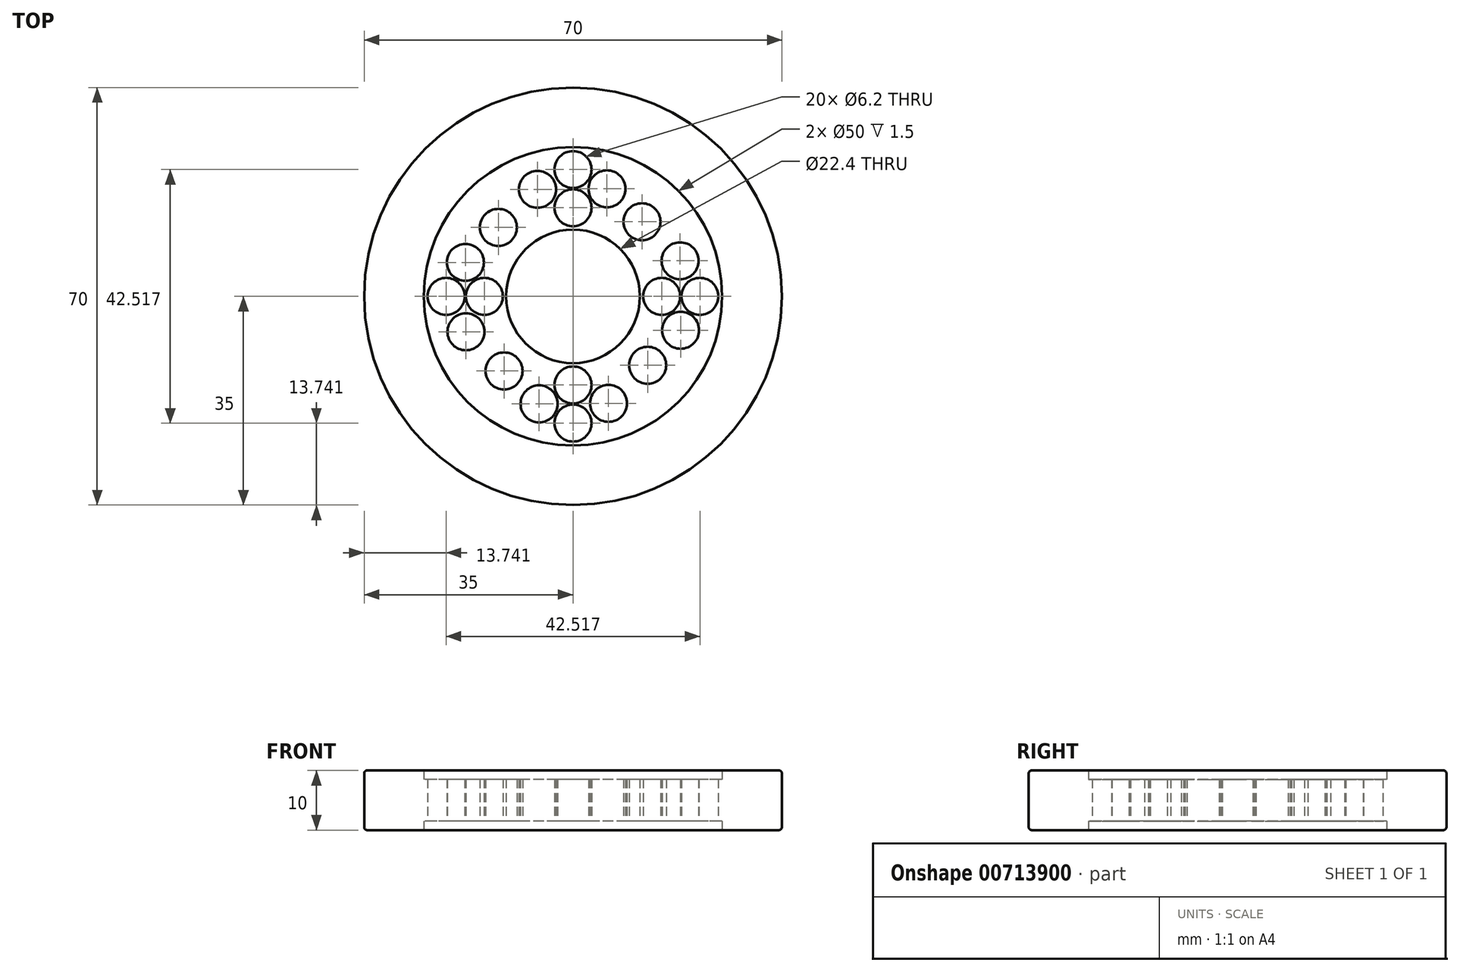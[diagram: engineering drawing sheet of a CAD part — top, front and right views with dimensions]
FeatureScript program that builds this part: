
annotation { "Feature Type Name" : "Feature", "Feature Type Description" : "" }
export const myFeature = defineFeature(function(context is Context, id is Id, definition is map)
    precondition{}
    {
        {
            var Q0;
            Q0=qCreatedBy(makeId("Top.planeOp"),FACE);
            var sketch = newSketch(context, id + "F0", { "sketchPlane" : qUnion([Q0])});
            skCircle(sketch, "E0", {"center": v(0, 0) * mm, "radius": 25 * mm});
            skCircle(sketch, "E1", {"center": v(0, 0) * mm, "radius": 35 * mm});
            skSolve(sketch);
        }
        {
            var Q0;
            Q0=qCreatedBy(makeId("Top.planeOp"),FACE);
            var sketch = newSketch(context, id + "F1", { "sketchPlane" : qUnion([Q0])});
            skCircle(sketch, "E2", {"center": v(0, 0) * mm, "radius": 11.2 * mm});
            skCircle(sketch, "E3", {"center": v(0, 0) * mm, "radius": 25 * mm});
            skCircle(sketch, "E4", {"center": v(-21.26, 0) * mm, "radius": 3.1 * mm});
            skCircle(sketch, "E5.1.0", {"center": v(0, -21.26) * mm, "radius": 3.1 * mm});
            skCircle(sketch, "E5.2.0", {"center": v(21.26, 0) * mm, "radius": 3.1 * mm});
            skCircle(sketch, "E5.3.0", {"center": v(0, 21.26) * mm, "radius": 3.1 * mm});
            skCircle(sketch, "E6", {"center": v(-14.86, 0) * mm, "radius": 3.1 * mm});
            skCircle(sketch, "E7.1.0", {"center": v(0, -14.86) * mm, "radius": 3.1 * mm});
            skCircle(sketch, "E7.2.0", {"center": v(14.86, 0) * mm, "radius": 3.1 * mm});
            skCircle(sketch, "E7.3.0", {"center": v(0, 14.86) * mm, "radius": 3.1 * mm});
            skCircle(sketch, "E8", {"center": v(-12.5, 11.56) * mm, "radius": 3.1 * mm});
            skCircle(sketch, "E9", {"center": v(-5.95, 17.94) * mm, "radius": 3.1 * mm});
            skCircle(sketch, "E10", {"center": v(-18.03, 5.7) * mm, "radius": 3.1 * mm});
            skCircle(sketch, "E11.1.0", {"center": v(-11.56, -12.5) * mm, "radius": 3.1 * mm});
            skCircle(sketch, "E11.2.0", {"center": v(12.5, -11.56) * mm, "radius": 3.1 * mm});
            skCircle(sketch, "E11.3.0", {"center": v(11.56, 12.5) * mm, "radius": 3.1 * mm});
            skCircle(sketch, "E12.1.0", {"center": v(-5.7, -18.03) * mm, "radius": 3.1 * mm});
            skCircle(sketch, "E12.2.0", {"center": v(18.03, -5.7) * mm, "radius": 3.1 * mm});
            skCircle(sketch, "E12.3.0", {"center": v(5.7, 18.03) * mm, "radius": 3.1 * mm});
            skCircle(sketch, "E13.1.0", {"center": v(-17.94, -5.95) * mm, "radius": 3.1 * mm});
            skCircle(sketch, "E13.2.0", {"center": v(5.95, -17.94) * mm, "radius": 3.1 * mm});
            skCircle(sketch, "E13.3.0", {"center": v(17.94, 5.95) * mm, "radius": 3.1 * mm});
            skSolve(sketch);
        }
        {
            var Q0;
            Q0=makeQuery(id+"F0.imprint","IMPRINT",FACE,{"disambiguationData":[TD([[makeQuery(id+"F0.imprint","IMPRINT",EDGE,{"derivedFrom":sQuery(id+"F0.wireOp",EDGE,"E0")}),-1.0]])]});
            extrude(context, id + "F2", {"entities" : qUnion([Q0]), "depth" : 5 * mm, "offsetDistance" : 25 * mm, "hasSecondDirection" : true, "secondDirectionOppositeDirection" : true, "secondDirectionDepth" : 5 * mm});
        }
        {
            var Q0;
            Q0 = qSketchRegion(id + "F1", true);
            extrude(context, id + "F3", {"entities" : qUnion([Q0]), "operationType" : NewBodyOperationType.ADD, "depth" : 3.5 * mm, "offsetDistance" : 25 * mm, "hasSecondDirection" : true, "secondDirectionOppositeDirection" : true, "secondDirectionDepth" : 3.5 * mm});
        }
        {
            var Q0;
            Q0=makeQuery(id+"F2.opExtrude","SWEPT_FACE",FACE,{"disambiguationData":[OSD([sQuery(id+"F0.wireOp",EDGE,"E1")])]});
            fillet(context, id + "F4", {"entities" : qUnion([Q0]), "radius" : 0.5 * mm, "tangentPropagation" : true, "allowEdgeOverflow" : false});
        }
    });
